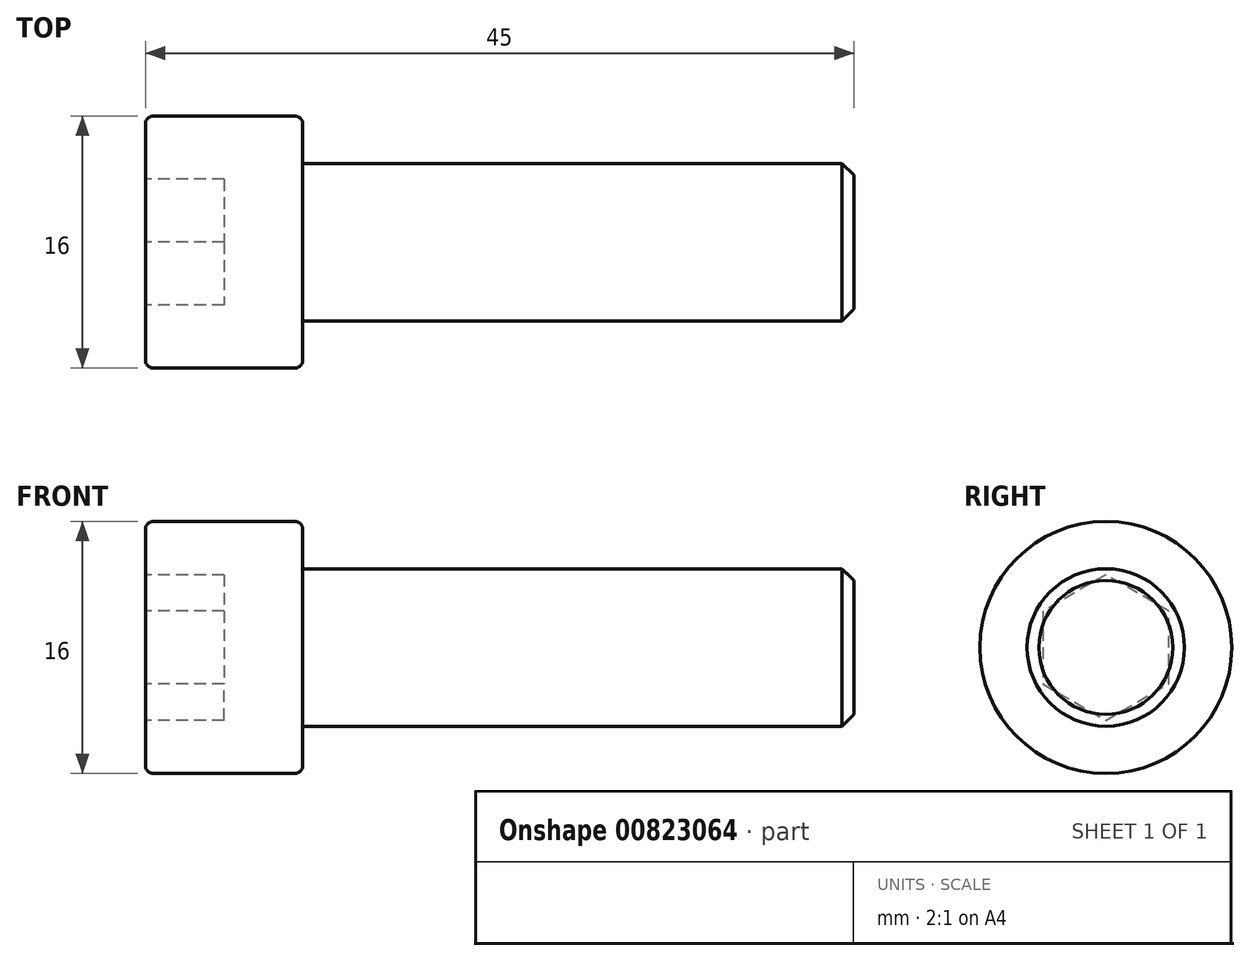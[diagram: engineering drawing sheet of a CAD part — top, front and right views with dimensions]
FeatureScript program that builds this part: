
annotation { "Feature Type Name" : "Feature", "Feature Type Description" : "" }
export const myFeature = defineFeature(function(context is Context, id is Id, definition is map)
    precondition{}
    {
        {
            var Q0;
            Q0=qCreatedBy(makeId("Front.planeOp"),FACE);
            var sketch = newSketch(context, id + "F0", { "sketchPlane" : qUnion([Q0])});
            skLineSegment(sketch, "E0", {"start": v(0, 0) * mm, "end": v(0, 5) * mm});
            skLineSegment(sketch, "E1", {"start": v(0, 5) * mm, "end": v(-35, 5) * mm});
            skLineSegment(sketch, "E2", {"start": v(-35, 5) * mm, "end": v(-35, 8) * mm});
            skLineSegment(sketch, "E3", {"start": v(-35, 8) * mm, "end": v(-45, 8) * mm});
            skLineSegment(sketch, "E4", {"start": v(-45, 8) * mm, "end": v(-45, 0) * mm});
            skLineSegment(sketch, "E5", {"start": v(-45, 0) * mm, "end": v(0, 0) * mm});
            skLineSegment(sketch, "E6", {"start": v(0, 0) * mm, "end": v(7.25, 0) * mm, "construction": true});
            skSolve(sketch);
        }
        {
            var Q0;
            Q0=makeQuery(id+"F0.imprint","IMPRINT",FACE,{"disambiguationData":[TD([[makeQuery(id+"F0.imprint","IMPRINT",EDGE,{"derivedFrom":sQuery(id+"F0.wireOp",EDGE,"E0")}),1.0]])]});
            var Q1;
            Q1=sQuery(id+"F0.wireOp",EDGE,"E6");
            revolve(context, id + "F1", {"surfaceOperationType" : NewSurfaceOperationType.NEW, "entities" : qUnion([Q0]), "axis" : qUnion([Q1]), "revolveType" : RevolveType.FULL});
        }
        {
            var Q0;
            Q0=makeQuery(id+"F1.opRevolve","SWEPT_EDGE",EDGE,{"disambiguationData":[OSD([sQuery(id+"F0.wireOp",EDGE,"E0"),sQuery(id+"F0.wireOp",EDGE,"E1")])]});
            chamfer(context, id + "F2", {"entities" : qUnion([Q0]), "width" : 0.75 * mm, "tangentPropagation" : true});
        }
        {
            var Q0;
            Q0=makeQuery(id+"F1.opRevolve","SWEPT_FACE",FACE,{"disambiguationData":[OSD([sQuery(id+"F0.wireOp",EDGE,"E3")])]});
            fillet(context, id + "F3", {"entities" : qUnion([Q0]), "radius" : 0.5 * mm, "tangentPropagation" : true, "allowEdgeOverflow" : false});
        }
        {
            var Q0;
            Q0=makeQuery(id+"F1.opRevolve","SWEPT_FACE",FACE,{"disambiguationData":[OSD([sQuery(id+"F0.wireOp",EDGE,"E4")])]});
            var sketch = newSketch(context, id + "F4", { "sketchPlane" : qUnion([Q0])});
            skLineSegment(sketch, "E7", {"start": v(0, 0) * mm, "end": v(7.18, 0) * mm, "construction": true});
            skCircle(sketch, "E8.cCircle", {"center": v(0, 0) * mm, "radius": 4 * mm, "construction": true});
            skLineSegment(sketch, "E8.0", {"start": v(4, 2.3) * mm, "end": v(4, -2.3) * mm});
            skLineSegment(sketch, "E8.1", {"start": v(4, -2.3) * mm, "end": v(0, -4.62) * mm});
            skLineSegment(sketch, "E8.2", {"start": v(0, -4.62) * mm, "end": v(-4, -2.3) * mm});
            skLineSegment(sketch, "E8.3", {"start": v(-4, -2.3) * mm, "end": v(-4, 2.3) * mm});
            skLineSegment(sketch, "E8.4", {"start": v(-4, 2.3) * mm, "end": v(0, 4.62) * mm});
            skLineSegment(sketch, "E8.5", {"start": v(0, 4.62) * mm, "end": v(4, 2.3) * mm});
            skPoint(sketch, "E8.0.midPoint", {"position": v(4, 0) * mm});
            skSolve(sketch);
        }
        {
            var Q0;
            Q0 = qSketchRegion(id + "F4", true);
            extrude(context, id + "F5", {"entities" : qUnion([Q0]), "operationType" : NewBodyOperationType.REMOVE, "oppositeDirection" : true, "depth" : 5 * mm, "offsetDistance" : 25 * mm});
        }
    });
